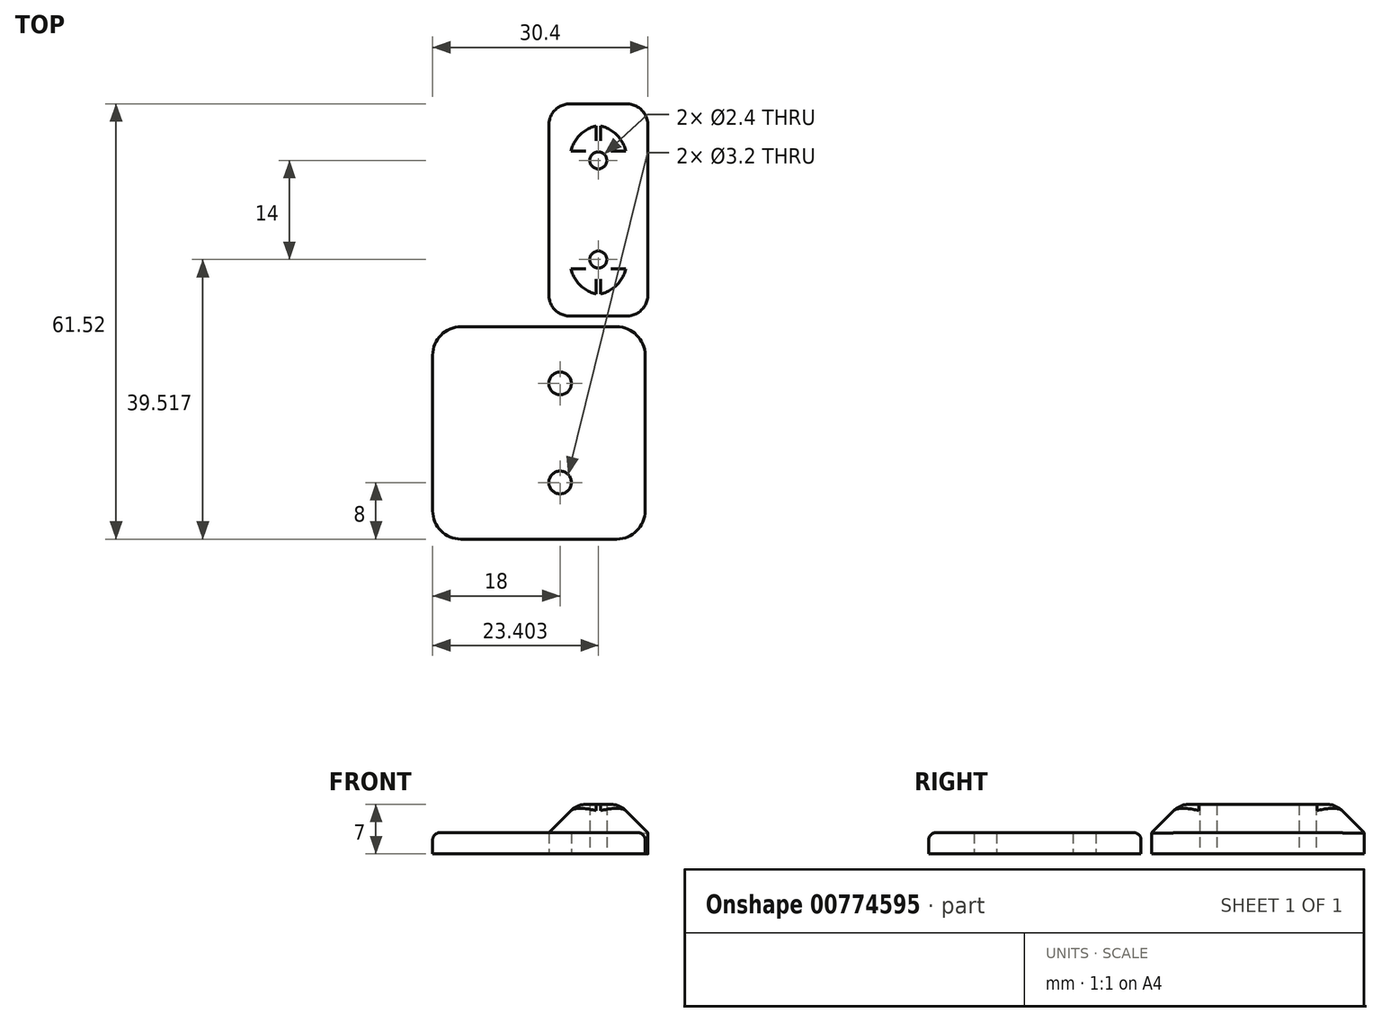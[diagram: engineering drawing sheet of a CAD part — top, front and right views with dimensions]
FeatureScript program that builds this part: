
annotation { "Feature Type Name" : "Feature", "Feature Type Description" : "" }
export const myFeature = defineFeature(function(context is Context, id is Id, definition is map)
    precondition{}
    {
        {
            var Q0;
            Q0=qCreatedBy(makeId("Top.planeOp"),FACE);
            var sketch = newSketch(context, id + "F0", { "sketchPlane" : qUnion([Q0])});
            skLineSegment(sketch, "E0.bottom", {"start": v(-15, 0) * mm, "end": v(15, 0) * mm});
            skLineSegment(sketch, "E0.top", {"start": v(-15, -30) * mm, "end": v(15, -30) * mm});
            skLineSegment(sketch, "E0.left", {"start": v(-15, 0) * mm, "end": v(-15, -30) * mm});
            skLineSegment(sketch, "E0.right", {"start": v(15, 0) * mm, "end": v(15, -30) * mm});
            skCircle(sketch, "E1", {"center": v(3, -8) * mm, "radius": 1.6 * mm});
            skCircle(sketch, "E2", {"center": v(3, -22) * mm, "radius": 1.6 * mm});
            skLineSegment(sketch, "E3", {"start": v(3, 0) * mm, "end": v(3, -30) * mm, "construction": true});
            skSolve(sketch);
        }
        {
            var Q0;
            Q0=makeQuery(id+"F0.imprint","IMPRINT",FACE,{"disambiguationData":[TD([[makeQuery(id+"F0.imprint","IMPRINT",EDGE,{"derivedFrom":sQuery(id+"F0.wireOp",EDGE,"E0.bottom")}),-1.0]])]});
            extrude(context, id + "F1", {"entities" : qUnion([Q0]), "depth" : 3 * mm, "offsetDistance" : 25 * mm});
        }
        {
            var Q0;
            Q0=makeQuery(id+"F1.opExtrude","SWEPT_EDGE",EDGE,{"disambiguationData":[OSD([sQuery(id+"F0.wireOp",EDGE,"E0.top"),sQuery(id+"F0.wireOp",EDGE,"E0.right")])]});
            var Q1;
            Q1=makeQuery(id+"F1.opExtrude","SWEPT_EDGE",EDGE,{"disambiguationData":[OSD([sQuery(id+"F0.wireOp",EDGE,"E0.bottom"),sQuery(id+"F0.wireOp",EDGE,"E0.right")])]});
            var Q2;
            Q2=makeQuery(id+"F1.opExtrude","SWEPT_EDGE",EDGE,{"disambiguationData":[OSD([sQuery(id+"F0.wireOp",EDGE,"E0.top"),sQuery(id+"F0.wireOp",EDGE,"E0.left")])]});
            var Q3;
            Q3=makeQuery(id+"F1.opExtrude","SWEPT_EDGE",EDGE,{"disambiguationData":[OSD([sQuery(id+"F0.wireOp",EDGE,"E0.bottom"),sQuery(id+"F0.wireOp",EDGE,"E0.left")])]});
            fillet(context, id + "F2", {"entities" : qUnion([Q0, Q1, Q2, Q3]), "radius" : 4 * mm, "tangentPropagation" : true, "allowEdgeOverflow" : false});
        }
        {
            var Q0;
            Q0=qCreatedBy(makeId("Top.planeOp"),FACE);
            var sketch = newSketch(context, id + "F3", { "sketchPlane" : qUnion([Q0])});
            skLineSegment(sketch, "E4.bottom", {"start": v(1.4, 1.52) * mm, "end": v(15.4, 1.52) * mm});
            skLineSegment(sketch, "E4.top", {"start": v(1.4, 31.52) * mm, "end": v(15.4, 31.52) * mm});
            skLineSegment(sketch, "E4.left", {"start": v(1.4, 1.52) * mm, "end": v(1.4, 31.52) * mm});
            skLineSegment(sketch, "E4.right", {"start": v(15.4, 1.52) * mm, "end": v(15.4, 31.52) * mm});
            skLineSegment(sketch, "E5", {"start": v(8.4, 1.52) * mm, "end": v(8.4, 31.52) * mm, "construction": true});
            skCircle(sketch, "E6", {"center": v(8.4, 23.52) * mm, "radius": 1.2 * mm});
            skCircle(sketch, "E7", {"center": v(8.4, 9.52) * mm, "radius": 1.2 * mm});
            skSolve(sketch);
        }
        {
            var Q0;
            Q0=makeQuery(id+"F3.imprint","IMPRINT",FACE,{"disambiguationData":[TD([[makeQuery(id+"F3.imprint","IMPRINT",EDGE,{"derivedFrom":sQuery(id+"F3.wireOp",EDGE,"E4.bottom")}),1.0]])]});
            extrude(context, id + "F4", {"entities" : qUnion([Q0]), "depth" : 7 * mm, "offsetDistance" : 25 * mm});
        }
        {
            var Q0;
            Q0=makeQuery(id+"F4.opExtrude","CAP_EDGE",EDGE,{"disambiguationData":[OSD([sQuery(id+"F3.wireOp",EDGE,"E4.right")])],"isStart":false});
            var Q1;
            Q1=makeQuery(id+"F4.opExtrude","CAP_EDGE",EDGE,{"disambiguationData":[OSD([sQuery(id+"F3.wireOp",EDGE,"E4.left")])],"isStart":false});
            var Q2;
            Q2=makeQuery(id+"F4.opExtrude","CAP_EDGE",EDGE,{"disambiguationData":[OSD([sQuery(id+"F3.wireOp",EDGE,"E4.bottom")])],"isStart":false});
            var Q3;
            Q3=makeQuery(id+"F4.opExtrude","CAP_EDGE",EDGE,{"disambiguationData":[OSD([sQuery(id+"F3.wireOp",EDGE,"E4.top")])],"isStart":false});
            chamfer(context, id + "F5", {"entities" : qUnion([Q0, Q1, Q2, Q3]), "width" : 4 * mm, "tangentPropagation" : true});
        }
        {
            var Q0;
            Q0=makeQuery(id+"F4.opExtrude","SWEPT_EDGE",EDGE,{"disambiguationData":[OSD([sQuery(id+"F3.wireOp",EDGE,"E4.bottom"),sQuery(id+"F3.wireOp",EDGE,"E4.left")])]});
            var Q1;
            Q1=makeQuery(id+"F4.opExtrude","SWEPT_EDGE",EDGE,{"disambiguationData":[OSD([sQuery(id+"F3.wireOp",EDGE,"E4.bottom"),sQuery(id+"F3.wireOp",EDGE,"E4.right")])]});
            var Q2;
            Q2=makeQuery(id+"F4.opExtrude","SWEPT_EDGE",EDGE,{"disambiguationData":[OSD([sQuery(id+"F3.wireOp",EDGE,"E4.top"),sQuery(id+"F3.wireOp",EDGE,"E4.right")])]});
            var Q3;
            Q3=makeQuery(id+"F4.opExtrude","SWEPT_EDGE",EDGE,{"disambiguationData":[OSD([sQuery(id+"F3.wireOp",EDGE,"E4.top"),sQuery(id+"F3.wireOp",EDGE,"E4.left")])]});
            var Q4;
            {var subQ0=sQuery(id+"F3.wireOp",EDGE,"E4.right");Q4=makeQuery(id+"F5.opChamfer","BLEND_EDGE",EDGE,{"blendedFrom":[makeQuery(id+"F4.opExtrude","CAP_EDGE",EDGE,{"disambiguationData":[OSD([subQ0])],"isStart":false}),makeQuery(id+"F4.opExtrude","CAP_FACE",FACE,{"disambiguationData":[OSD([sQuery(id+"F3.wireOp",EDGE,"E4.bottom"),sQuery(id+"F3.wireOp",EDGE,"E4.top"),sQuery(id+"F3.wireOp",EDGE,"E4.left"),subQ0,sQuery(id+"F3.wireOp",EDGE,"E6"),sQuery(id+"F3.wireOp",EDGE,"E7")])],"isStart":false})],"blendedInto":[makeQuery(id+"F4.opExtrude","CAP_FACE",FACE,{"disambiguationData":[OSD([sQuery(id+"F3.wireOp",EDGE,"E4.bottom"),sQuery(id+"F3.wireOp",EDGE,"E4.top"),sQuery(id+"F3.wireOp",EDGE,"E4.left"),subQ0,sQuery(id+"F3.wireOp",EDGE,"E6"),sQuery(id+"F3.wireOp",EDGE,"E7")])],"isStart":false})]});}
            var Q5;
            {var subQ0=sQuery(id+"F3.wireOp",EDGE,"E4.left");Q5=makeQuery(id+"F5.opChamfer","BLEND_EDGE",EDGE,{"blendedFrom":[makeQuery(id+"F4.opExtrude","CAP_EDGE",EDGE,{"disambiguationData":[OSD([subQ0])],"isStart":false}),makeQuery(id+"F4.opExtrude","CAP_FACE",FACE,{"disambiguationData":[OSD([sQuery(id+"F3.wireOp",EDGE,"E4.bottom"),sQuery(id+"F3.wireOp",EDGE,"E4.top"),subQ0,sQuery(id+"F3.wireOp",EDGE,"E4.right"),sQuery(id+"F3.wireOp",EDGE,"E6"),sQuery(id+"F3.wireOp",EDGE,"E7")])],"isStart":false})],"blendedInto":[makeQuery(id+"F4.opExtrude","CAP_FACE",FACE,{"disambiguationData":[OSD([sQuery(id+"F3.wireOp",EDGE,"E4.bottom"),sQuery(id+"F3.wireOp",EDGE,"E4.top"),subQ0,sQuery(id+"F3.wireOp",EDGE,"E4.right"),sQuery(id+"F3.wireOp",EDGE,"E6"),sQuery(id+"F3.wireOp",EDGE,"E7")])],"isStart":false})]});}
            var Q6;
            {var subQ0=sQuery(id+"F3.wireOp",EDGE,"E4.top");Q6=makeQuery(id+"F5.opChamfer","BLEND_EDGE",EDGE,{"blendedFrom":[makeQuery(id+"F4.opExtrude","CAP_EDGE",EDGE,{"disambiguationData":[OSD([subQ0])],"isStart":false}),makeQuery(id+"F4.opExtrude","CAP_FACE",FACE,{"disambiguationData":[OSD([sQuery(id+"F3.wireOp",EDGE,"E4.bottom"),subQ0,sQuery(id+"F3.wireOp",EDGE,"E4.left"),sQuery(id+"F3.wireOp",EDGE,"E4.right"),sQuery(id+"F3.wireOp",EDGE,"E6"),sQuery(id+"F3.wireOp",EDGE,"E7")])],"isStart":false})],"blendedInto":[makeQuery(id+"F4.opExtrude","CAP_FACE",FACE,{"disambiguationData":[OSD([sQuery(id+"F3.wireOp",EDGE,"E4.bottom"),subQ0,sQuery(id+"F3.wireOp",EDGE,"E4.left"),sQuery(id+"F3.wireOp",EDGE,"E4.right"),sQuery(id+"F3.wireOp",EDGE,"E6"),sQuery(id+"F3.wireOp",EDGE,"E7")])],"isStart":false})]});}
            var Q7;
            {var subQ0=sQuery(id+"F3.wireOp",EDGE,"E4.bottom");Q7=makeQuery(id+"F5.opChamfer","BLEND_EDGE",EDGE,{"blendedFrom":[makeQuery(id+"F4.opExtrude","CAP_EDGE",EDGE,{"disambiguationData":[OSD([subQ0])],"isStart":false}),makeQuery(id+"F4.opExtrude","CAP_FACE",FACE,{"disambiguationData":[OSD([subQ0,sQuery(id+"F3.wireOp",EDGE,"E4.top"),sQuery(id+"F3.wireOp",EDGE,"E4.left"),sQuery(id+"F3.wireOp",EDGE,"E4.right"),sQuery(id+"F3.wireOp",EDGE,"E6"),sQuery(id+"F3.wireOp",EDGE,"E7")])],"isStart":false})],"blendedInto":[makeQuery(id+"F4.opExtrude","CAP_FACE",FACE,{"disambiguationData":[OSD([subQ0,sQuery(id+"F3.wireOp",EDGE,"E4.top"),sQuery(id+"F3.wireOp",EDGE,"E4.left"),sQuery(id+"F3.wireOp",EDGE,"E4.right"),sQuery(id+"F3.wireOp",EDGE,"E6"),sQuery(id+"F3.wireOp",EDGE,"E7")])],"isStart":false})]});}
            fillet(context, id + "F6", {"entities" : qUnion([Q0, Q1, Q2, Q3, Q4, Q5, Q6, Q7]), "radius" : 3 * mm, "tangentPropagation" : true, "allowEdgeOverflow" : false});
        }
        {
            var Q0;
            Q0=makeQuery(id+"F5.opChamfer","BLEND_EDGE",EDGE,{"blendedFrom":[makeQuery(id+"F4.opExtrude","CAP_EDGE",EDGE,{"disambiguationData":[OSD([sQuery(id+"F3.wireOp",EDGE,"E4.bottom")])],"isStart":false}),makeQuery(id+"F4.opExtrude","CAP_EDGE",EDGE,{"disambiguationData":[OSD([sQuery(id+"F3.wireOp",EDGE,"E4.right")])],"isStart":false})],"blendedInto":[]});
            var Q1;
            Q1=makeQuery(id+"F5.opChamfer","BLEND_EDGE",EDGE,{"blendedFrom":[makeQuery(id+"F4.opExtrude","CAP_EDGE",EDGE,{"disambiguationData":[OSD([sQuery(id+"F3.wireOp",EDGE,"E4.bottom")])],"isStart":false}),makeQuery(id+"F4.opExtrude","CAP_EDGE",EDGE,{"disambiguationData":[OSD([sQuery(id+"F3.wireOp",EDGE,"E4.left")])],"isStart":false})],"blendedInto":[]});
            var Q2;
            Q2=makeQuery(id+"F5.opChamfer","BLEND_EDGE",EDGE,{"blendedFrom":[makeQuery(id+"F4.opExtrude","CAP_EDGE",EDGE,{"disambiguationData":[OSD([sQuery(id+"F3.wireOp",EDGE,"E4.top")])],"isStart":false}),makeQuery(id+"F4.opExtrude","CAP_EDGE",EDGE,{"disambiguationData":[OSD([sQuery(id+"F3.wireOp",EDGE,"E4.left")])],"isStart":false})],"blendedInto":[]});
            var Q3;
            Q3=makeQuery(id+"F5.opChamfer","BLEND_EDGE",EDGE,{"blendedFrom":[makeQuery(id+"F4.opExtrude","CAP_EDGE",EDGE,{"disambiguationData":[OSD([sQuery(id+"F3.wireOp",EDGE,"E4.top")])],"isStart":false}),makeQuery(id+"F4.opExtrude","CAP_EDGE",EDGE,{"disambiguationData":[OSD([sQuery(id+"F3.wireOp",EDGE,"E4.right")])],"isStart":false})],"blendedInto":[]});
            fillet(context, id + "F7", {"entities" : qUnion([Q0, Q1, Q2, Q3]), "radius" : 5 * mm, "tangentPropagation" : true, "allowEdgeOverflow" : false});
        }
        {
            var Q0;
            Q0=makeQuery(id+"F1.opExtrude","CAP_EDGE",EDGE,{"disambiguationData":[OSD([sQuery(id+"F0.wireOp",EDGE,"E0.bottom")])],"isStart":false});
            fillet(context, id + "F8", {"entities" : qUnion([Q0]), "radius" : 1 * mm, "tangentPropagation" : true, "allowEdgeOverflow" : false});
        }
    });
